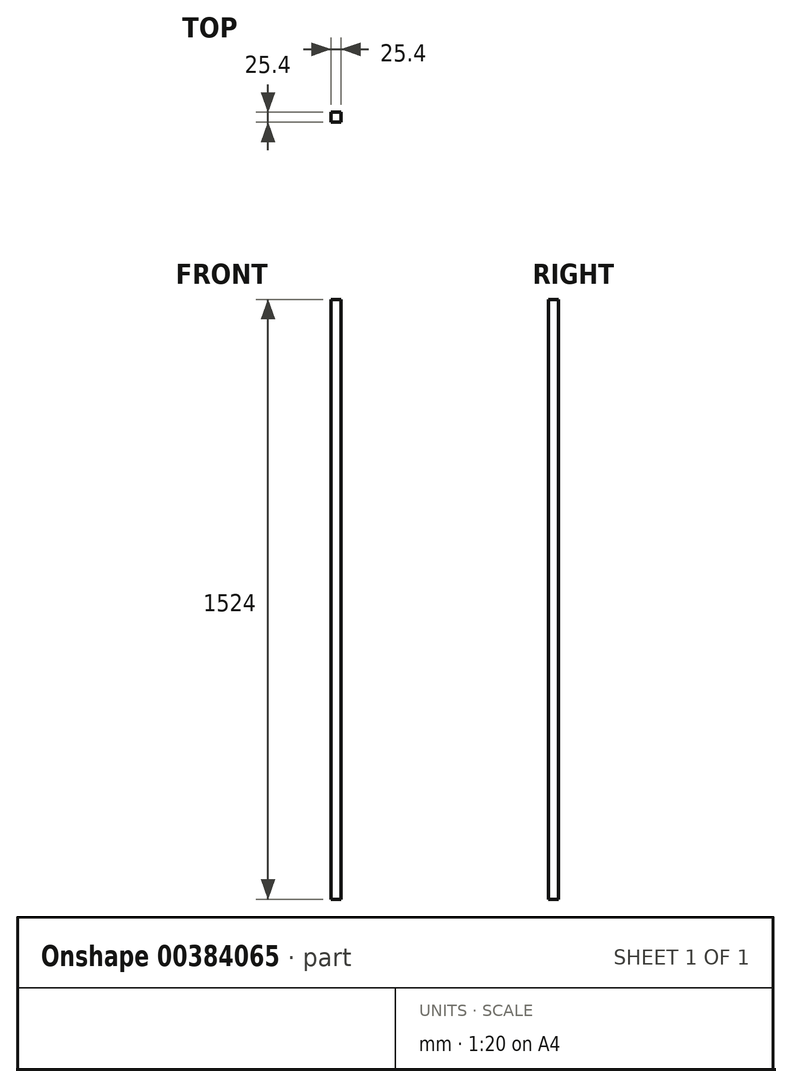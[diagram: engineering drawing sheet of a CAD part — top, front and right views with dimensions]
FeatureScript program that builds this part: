
annotation { "Feature Type Name" : "Feature", "Feature Type Description" : "" }
export const myFeature = defineFeature(function(context is Context, id is Id, definition is map)
    precondition{}
    {
        {
            var Q0;
            Q0=qCreatedBy(makeId("Top.planeOp"),FACE);
            var sketch = newSketch(context, id + "F0", { "sketchPlane" : qUnion([Q0])});
            skLineSegment(sketch, "E0.bottom", {"start": v(0, 0) * mm, "end": v(25.4, 0) * mm});
            skLineSegment(sketch, "E0.top", {"start": v(0, 25.4) * mm, "end": v(25.4, 25.4) * mm});
            skLineSegment(sketch, "E0.left", {"start": v(0, 0) * mm, "end": v(0, 25.4) * mm});
            skLineSegment(sketch, "E0.right", {"start": v(25.4, 0) * mm, "end": v(25.4, 25.4) * mm});
            skSolve(sketch);
        }
        {
            var Q0;
            Q0=makeQuery(id+"F0.imprint","IMPRINT",FACE,{"disambiguationData":[TD([[makeQuery(id+"F0.imprint","IMPRINT",EDGE,{"derivedFrom":sQuery(id+"F0.wireOp",EDGE,"E0.bottom")}),1.0]])]});
            extrude(context, id + "F1", {"entities" : qUnion([Q0]), "depth" : 1524 * mm});
        }
    });
